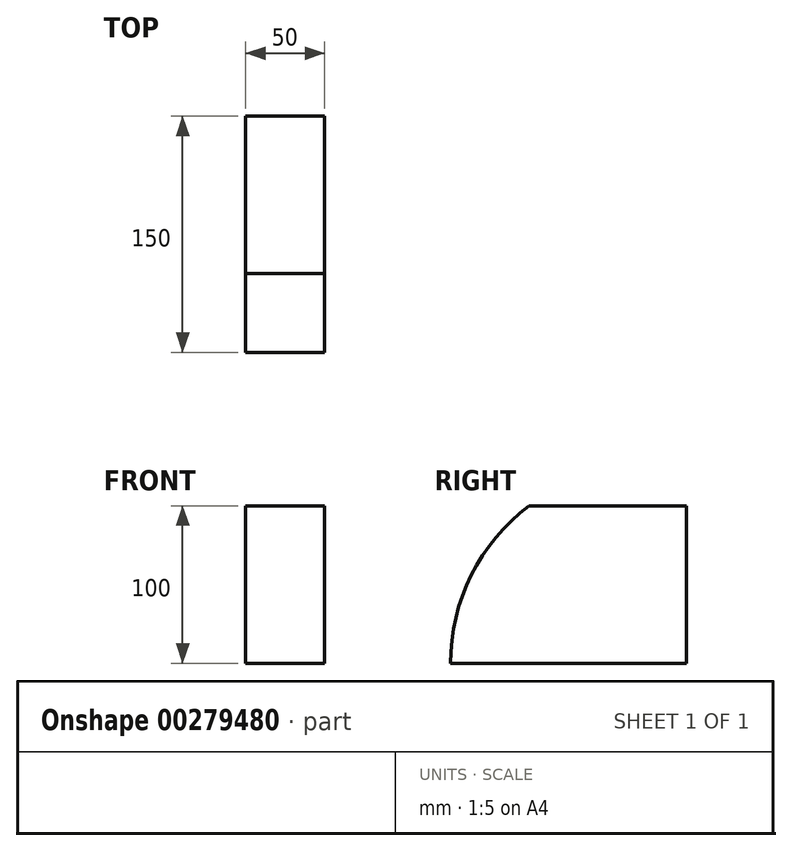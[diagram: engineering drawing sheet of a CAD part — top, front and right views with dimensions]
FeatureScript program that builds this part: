
annotation { "Feature Type Name" : "Feature", "Feature Type Description" : "" }
export const myFeature = defineFeature(function(context is Context, id is Id, definition is map)
    precondition{}
    {
        {
            var Q0;
            Q0=qCreatedBy(makeId("Right.planeOp"),FACE);
            var sketch = newSketch(context, id + "F0", { "sketchPlane" : qUnion([Q0])});
            skLineSegment(sketch, "E0.bottom", {"start": v(-4.56, 51.74) * mm, "end": v(95.44, 51.74) * mm});
            skLineSegment(sketch, "E0.top", {"start": v(-54.56, -48.26) * mm, "end": v(95.44, -48.26) * mm});
            skLineSegment(sketch, "E0.right", {"start": v(95.44, 51.74) * mm, "end": v(95.44, -48.26) * mm});
            skArc(sketch, "E1", {"start": v(-4.56, 51.74) * mm, "mid": v(-41.36, 7.64) * mm, "end": v(-54.56, -48.26) * mm});
            skSolve(sketch);
        }
        {
            var Q0;
            Q0=makeQuery(id+"F0.imprint","IMPRINT",FACE,{"disambiguationData":[TD([[makeQuery(id+"F0.imprint","IMPRINT",EDGE,{"derivedFrom":sQuery(id+"F0.wireOp",EDGE,"E0.bottom")}),-1.0]])]});
            extrude(context, id + "F1", {"entities" : qUnion([Q0]), "depth" : 50 * mm});
        }
    });
